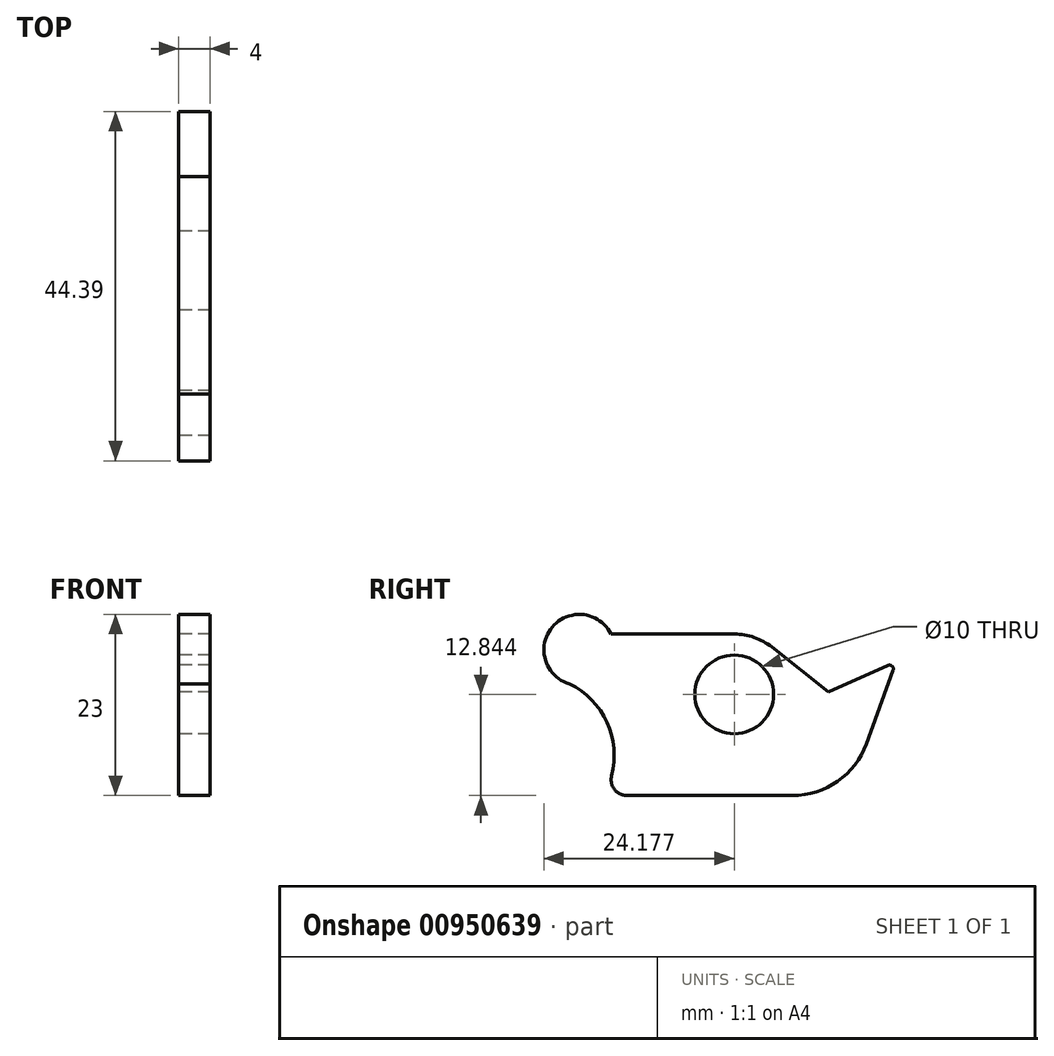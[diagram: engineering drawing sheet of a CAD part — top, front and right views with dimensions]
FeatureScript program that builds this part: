
annotation { "Feature Type Name" : "Feature", "Feature Type Description" : "" }
export const myFeature = defineFeature(function(context is Context, id is Id, definition is map)
    precondition{}
    {
        {
            var Q0;
            Q0=qCreatedBy(makeId("Right.planeOp"),FACE);
            var sketch = newSketch(context, id + "F0", { "sketchPlane" : qUnion([Q0])});
            skLineSegment(sketch, "E0.bottom", {"start": v(-11.43, 0) * mm, "end": v(-32.47, 0) * mm});
            skLineSegment(sketch, "E0.right", {"start": v(-43, 0) * mm, "end": v(-43, 18.5) * mm});
            skLineSegment(sketch, "E1", {"start": v(-54.9, 7.5) * mm, "end": v(17.13, 7.5) * mm, "construction": true});
            skLineSegment(sketch, "E2", {"start": v(-18.82, 33.74) * mm, "end": v(-18.82, -18.05) * mm, "construction": true});
            skCircle(sketch, "E3", {"center": v(-18.82, 12.84) * mm, "radius": 5 * mm});
            skArc(sketch, "E4", {"start": v(-34.47, 20.5) * mm, "mid": v(-41.94, 21.4) * mm, "end": v(-39.78, 14.19) * mm});
            skLineSegment(sketch, "E5", {"start": v(-48.78, 20.5) * mm, "end": v(-18.82, 20.5) * mm, "construction": true});
            skLineSegment(sketch, "E6", {"start": v(-18.82, 20.5) * mm, "end": v(-34.47, 20.5) * mm});
            skLineSegment(sketch, "E7", {"start": v(0, 12.16) * mm, "end": v(-2.03, 6.58) * mm});
            skLineSegment(sketch, "E8", {"start": v(0, 12.16) * mm, "end": v(1.36, 15.89) * mm});
            skLineSegment(sketch, "E9", {"start": v(-11.75, 17) * mm, "end": v(-14.06, 18.84) * mm});
            skArc(sketch, "E10", {"start": v(-14.06, 18.84) * mm, "mid": v(-16.3, 20.07) * mm, "end": v(-18.82, 20.5) * mm});
            skArc(sketch, "E11.trimOffspring", {"start": v(-14.06, 18.84) * mm, "mid": v(-16.3, 20.07) * mm, "end": v(-18.82, 20.5) * mm, "construction": true});
            skLineSegment(sketch, "E12", {"start": v(0.68, 16.52) * mm, "end": v(-6.87, 13.13) * mm});
            skLineSegment(sketch, "E13", {"start": v(-11.75, 17) * mm, "end": v(-6.87, 13.13) * mm});
            skArc(sketch, "E14.filletArc", {"start": v(-4.46, 0) * mm, "mid": v(-4.43, 0) * mm, "end": v(-4.41, 0.03) * mm});
            skArc(sketch, "E15.filletArc", {"start": v(-11.43, 0) * mm, "mid": v(-5.7, 1.8) * mm, "end": v(-2.03, 6.58) * mm});
            skArc(sketch, "E16", {"start": v(-34.4, 2.5) * mm, "mid": v(-35, 9.3) * mm, "end": v(-39.78, 14.19) * mm});
            skArc(sketch, "E17.filletArc", {"start": v(-34.4, 2.5) * mm, "mid": v(-34.05, 0.78) * mm, "end": v(-32.47, 0) * mm});
            skPoint(sketch, "E18.visualSharp", {"position": v(1.76, 17) * mm});
            skArc(sketch, "E18.filletArc", {"start": v(1.36, 15.89) * mm, "mid": v(1.23, 16.43) * mm, "end": v(0.68, 16.52) * mm});
            skSolve(sketch);
        }
        {
            var Q0;
            Q0 = qSketchRegion(id + "F0", true);
            extrude(context, id + "F1", {"entities" : qUnion([Q0]), "depth" : 4 * mm, "offsetDistance" : 25 * mm});
        }
    });
